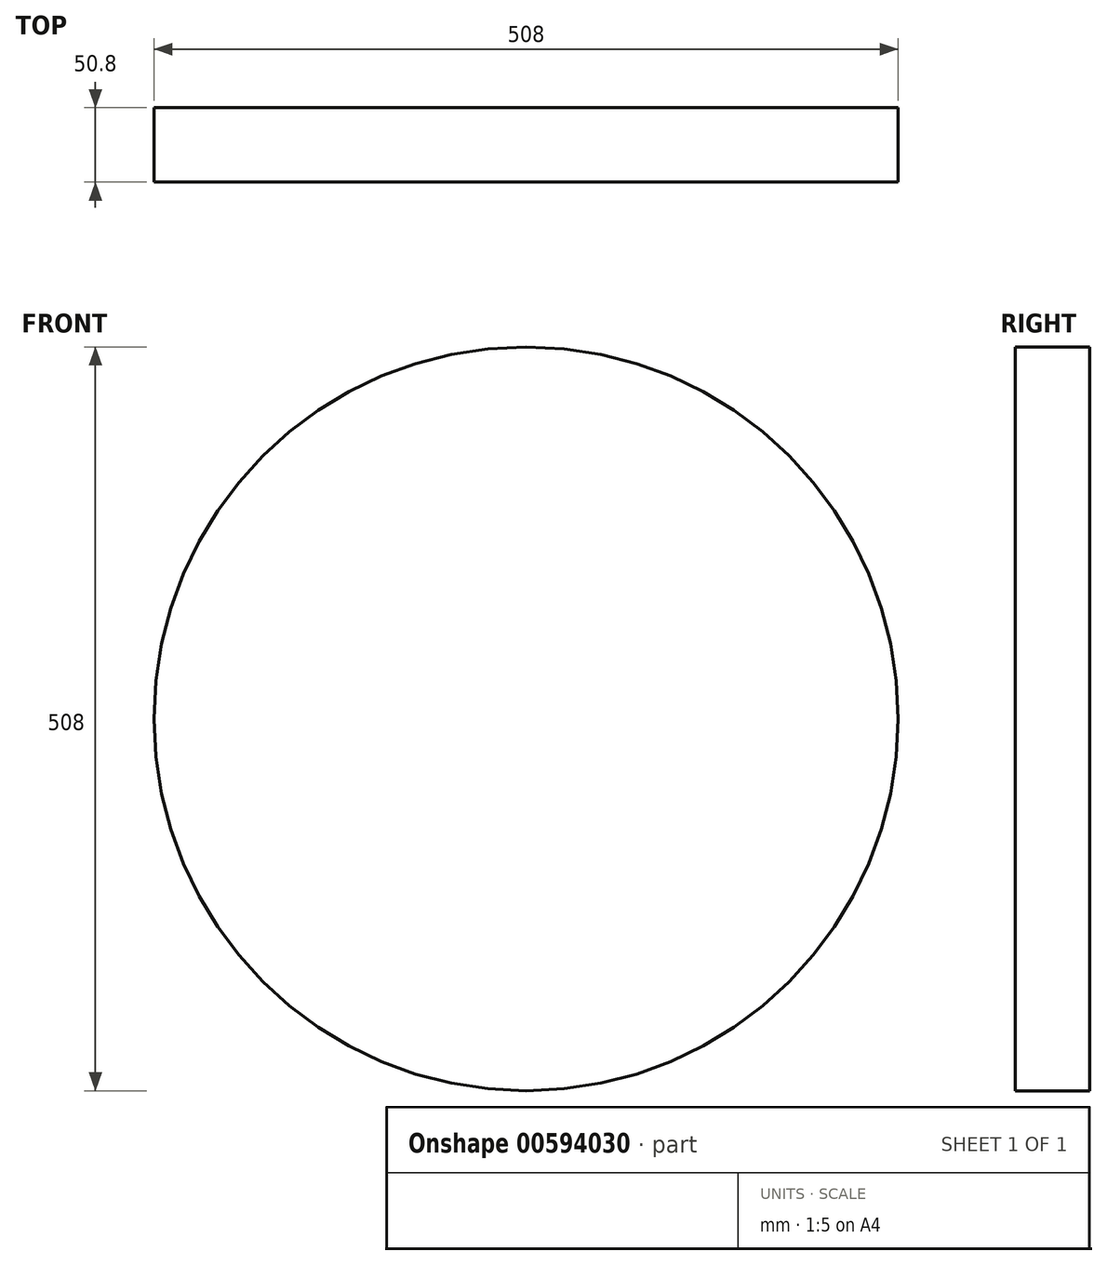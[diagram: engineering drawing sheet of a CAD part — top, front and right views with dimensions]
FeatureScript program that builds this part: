
annotation { "Feature Type Name" : "Feature", "Feature Type Description" : "" }
export const myFeature = defineFeature(function(context is Context, id is Id, definition is map)
    precondition{}
    {
        {
            var Q0;
            Q0=qCreatedBy(makeId("Front.planeOp"),FACE);
            var sketch = newSketch(context, id + "F0", { "sketchPlane" : qUnion([Q0])});
            skCircle(sketch, "E0", {"center": v(-239.32, 95.13) * mm, "radius": 254 * mm});
            skCircle(sketch, "E1", {"center": v(-239.32, 95.13) * mm, "radius": 16 * mm});
            skSolve(sketch);
        }
        {
            var Q0;
            Q0=makeQuery(id+"F0.imprint","IMPRINT",FACE,{"disambiguationData":[TD([[makeQuery(id+"F0.imprint","IMPRINT",EDGE,{"derivedFrom":sQuery(id+"F0.wireOp",EDGE,"E0")}),1.0]])]});
            var Q1;
            Q1=makeQuery(id+"F0.imprint","IMPRINT",FACE,{"disambiguationData":[TD([[makeQuery(id+"F0.imprint","IMPRINT",EDGE,{"derivedFrom":sQuery(id+"F0.wireOp",EDGE,"E1")}),1.0]])]});
            extrude(context, id + "F1", {"entities" : qUnion([Q0, Q1]), "depth" : 50.8 * mm, "offsetDistance" : 25.4 * mm});
        }
    });
